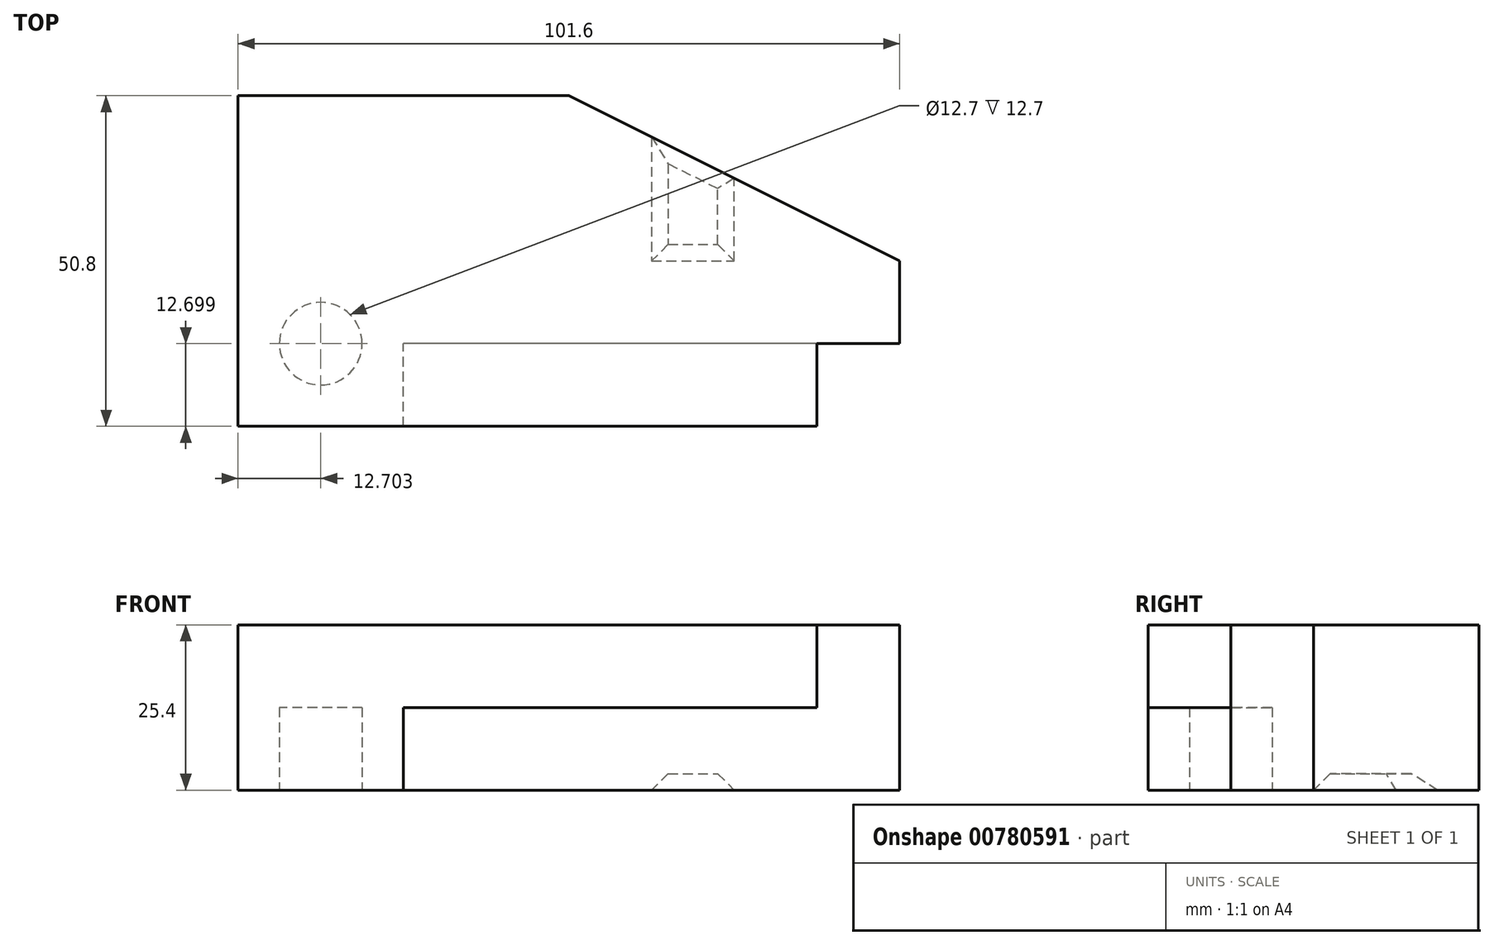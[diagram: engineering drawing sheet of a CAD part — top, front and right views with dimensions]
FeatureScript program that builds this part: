
annotation { "Feature Type Name" : "Feature", "Feature Type Description" : "" }
export const myFeature = defineFeature(function(context is Context, id is Id, definition is map)
    precondition{}
    {
        {
            var Q0;
            Q0=qCreatedBy(makeId("Top.planeOp"),FACE);
            var sketch = newSketch(context, id + "F0", { "sketchPlane" : qUnion([Q0])});
            skLineSegment(sketch, "E0", {"start": v(-40.76, -10.51) * mm, "end": v(-40.76, 40.29) * mm});
            skLineSegment(sketch, "E1", {"start": v(-40.76, 40.29) * mm, "end": v(10.04, 40.29) * mm});
            skLineSegment(sketch, "E2", {"start": v(-40.76, -10.51) * mm, "end": v(48.14, -10.51) * mm});
            skLineSegment(sketch, "E3", {"start": v(48.14, -10.51) * mm, "end": v(48.14, 2.19) * mm});
            skLineSegment(sketch, "E4", {"start": v(48.14, 2.19) * mm, "end": v(60.84, 2.19) * mm});
            skLineSegment(sketch, "E5", {"start": v(60.84, 2.19) * mm, "end": v(60.84, 14.89) * mm});
            skLineSegment(sketch, "E6", {"start": v(60.84, 14.89) * mm, "end": v(10.04, 40.29) * mm});
            skSolve(sketch);
        }
        {
            var Q0;
            Q0=qSketchRegion(id+"F0",true);
            extrude(context, id + "F1", {"entities" : qUnion([Q0]), "depth" : 12.7 * mm, "offsetDistance" : 25.4 * mm});
        }
        {
            var Q0;
            Q0=makeQuery(id+"F1.opExtrude","CAP_FACE",FACE,{"disambiguationData":[OSD([sQuery(id+"F0.wireOp",EDGE,"E0"),sQuery(id+"F0.wireOp",EDGE,"E1"),sQuery(id+"F0.wireOp",EDGE,"E2"),sQuery(id+"F0.wireOp",EDGE,"E3"),sQuery(id+"F0.wireOp",EDGE,"E4"),sQuery(id+"F0.wireOp",EDGE,"E5"),sQuery(id+"F0.wireOp",EDGE,"E6")])],"isStart":false});
            var sketch = newSketch(context, id + "F2", { "sketchPlane" : qUnion([Q0])});
            skLineSegment(sketch, "E7", {"start": v(-40.76, -10.51) * mm, "end": v(-15.36, -10.51) * mm});
            skLineSegment(sketch, "E8", {"start": v(-15.36, -10.51) * mm, "end": v(-15.36, 2.19) * mm});
            skLineSegment(sketch, "E9", {"start": v(48.14, 2.19) * mm, "end": v(-15.36, 2.19) * mm});
            skSolve(sketch);
        }
        {
            var Q0;
            Q0=makeQuery(id+"F2.imprint","IMPRINT",FACE,{"disambiguationData":[TD([[makeQuery(id+"F2.imprint","IMPRINT",EDGE,{"derivedFrom":sQuery(id+"F2.wireOp",EDGE,"E7")}),1.0]])]});
            extrude(context, id + "F3", {"entities" : qUnion([Q0]), "operationType" : NewBodyOperationType.ADD, "depth" : 12.7 * mm, "offsetDistance" : 25.4 * mm});
        }
        {
            var Q0;
            Q0=makeQuery(id+"F3.opExtrude","CAP_FACE",FACE,{"disambiguationData":[OSD([sQuery(id+"F0.wireOp",EDGE,"E0"),sQuery(id+"F0.wireOp",EDGE,"E1"),sQuery(id+"F0.wireOp",EDGE,"E4"),sQuery(id+"F0.wireOp",EDGE,"E5"),sQuery(id+"F0.wireOp",EDGE,"E6"),sQuery(id+"F2.wireOp",EDGE,"E7"),sQuery(id+"F2.wireOp",EDGE,"E8"),sQuery(id+"F2.wireOp",EDGE,"E9")])],"isStart":false});
            var sketch = newSketch(context, id + "F4", { "sketchPlane" : qUnion([Q0])});
            skLineSegment(sketch, "E10", {"start": v(-28.06, -10.51) * mm, "end": v(-28.06, 40.29) * mm, "construction": true});
            skLineSegment(sketch, "E11", {"start": v(-15.36, 2.19) * mm, "end": v(-40.76, 2.19) * mm, "construction": true});
            skCircle(sketch, "E12", {"center": v(-28.06, 2.19) * mm, "radius": 6.35 * mm});
            skSolve(sketch);
        }
        {
            var Q0;
            Q0=qSketchRegion(id+"F4",true);
            extrude(context, id + "F5", {"entities" : qUnion([Q0]), "operationType" : NewBodyOperationType.REMOVE, "oppositeDirection" : true, "depth" : 12.7 * mm, "offsetDistance" : 25.4 * mm});
        }
        {
            var Q0;
            Q0=makeQuery(id+"F3.opExtrude","CAP_FACE",FACE,{"disambiguationData":[OSD([sQuery(id+"F0.wireOp",EDGE,"E0"),sQuery(id+"F0.wireOp",EDGE,"E1"),sQuery(id+"F0.wireOp",EDGE,"E4"),sQuery(id+"F0.wireOp",EDGE,"E5"),sQuery(id+"F0.wireOp",EDGE,"E6"),sQuery(id+"F2.wireOp",EDGE,"E7"),sQuery(id+"F2.wireOp",EDGE,"E8"),sQuery(id+"F2.wireOp",EDGE,"E9")])],"isStart":false});
            var sketch = newSketch(context, id + "F6", { "sketchPlane" : qUnion([Q0])});
            skLineSegment(sketch, "E13", {"start": v(60.84, 14.89) * mm, "end": v(22.74, 14.89) * mm});
            skLineSegment(sketch, "E14", {"start": v(22.74, 14.89) * mm, "end": v(22.74, 33.94) * mm});
            skLineSegment(sketch, "E15", {"start": v(35.44, 27.59) * mm, "end": v(35.44, 14.89) * mm});
            skLineSegment(sketch, "E16", {"start": v(22.74, 33.94) * mm, "end": v(35.44, 27.59) * mm});
            skSolve(sketch);
        }
        {
            var Q0;
            Q0=qSketchRegion(id+"F6",true);
            extrude(context, id + "F7", {"entities" : qUnion([Q0]), "operationType" : NewBodyOperationType.REMOVE, "oppositeDirection" : true, "depth" : 2.54 * mm, "offsetDistance" : 25.4 * mm, "hasDraft" : true, "draftAngle" : 45 * degree, "draftPullDirection" : true});
        }
        {
            var Q0;
            Q0=makeQuery(id+"F1.opExtrude","SWEPT_BODY",BODY,{"disambiguationData":[OSD([sQuery(id+"F0.wireOp",EDGE,"E0"),sQuery(id+"F0.wireOp",EDGE,"E1"),sQuery(id+"F0.wireOp",EDGE,"E2"),sQuery(id+"F0.wireOp",EDGE,"E3"),sQuery(id+"F0.wireOp",EDGE,"E4"),sQuery(id+"F0.wireOp",EDGE,"E5"),sQuery(id+"F0.wireOp",EDGE,"E6")])]});
            var Q1;
            Q1=makeQuery(id+"F1.opExtrude","CAP_FACE",FACE,{"disambiguationData":[OSD([sQuery(id+"F0.wireOp",EDGE,"E0"),sQuery(id+"F0.wireOp",EDGE,"E1"),sQuery(id+"F0.wireOp",EDGE,"E2"),sQuery(id+"F0.wireOp",EDGE,"E3"),sQuery(id+"F0.wireOp",EDGE,"E4"),sQuery(id+"F0.wireOp",EDGE,"E5"),sQuery(id+"F0.wireOp",EDGE,"E6")])],"isStart":true});
            mirror(context, id + "F8", {"entities" : qUnion([Q0]), "mirrorPlane" : qUnion([Q1])});
        }
        {
            var Q0;
            Q0=makeQuery(id+"F1.opExtrude","SWEPT_BODY",BODY,{"disambiguationData":[OSD([sQuery(id+"F0.wireOp",EDGE,"E0"),sQuery(id+"F0.wireOp",EDGE,"E1"),sQuery(id+"F0.wireOp",EDGE,"E2"),sQuery(id+"F0.wireOp",EDGE,"E3"),sQuery(id+"F0.wireOp",EDGE,"E4"),sQuery(id+"F0.wireOp",EDGE,"E5"),sQuery(id+"F0.wireOp",EDGE,"E6")])]});
            deleteBodies(context, id + "F9", {"entities" : qUnion([Q0])});
        }
    });
